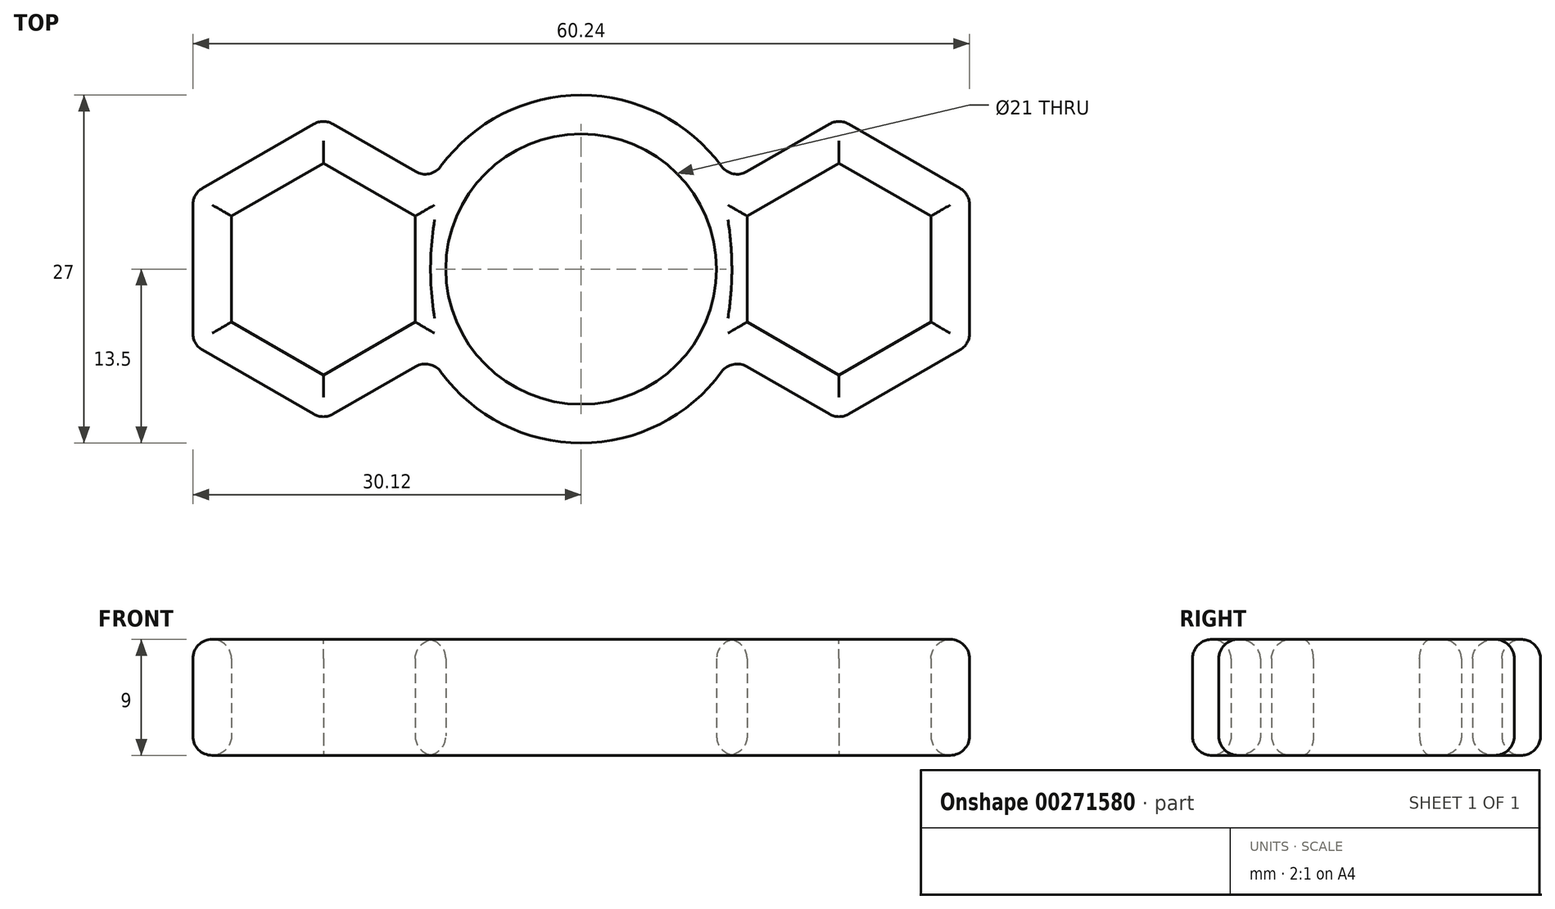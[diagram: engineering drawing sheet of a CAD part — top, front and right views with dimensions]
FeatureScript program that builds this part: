
annotation { "Feature Type Name" : "Feature", "Feature Type Description" : "" }
export const myFeature = defineFeature(function(context is Context, id is Id, definition is map)
    precondition{}
    {
        {
            var Q0;
            Q0=qCreatedBy(makeId("Top.planeOp"),FACE);
            var sketch = newSketch(context, id + "F0", { "sketchPlane" : qUnion([Q0])});
            skCircle(sketch, "E0", {"center": v(0, 0) * mm, "radius": 10.5 * mm});
            skCircle(sketch, "E1.cCircle", {"center": v(20, 0) * mm, "radius": 7.12 * mm, "construction": true});
            skLineSegment(sketch, "E1.0", {"start": v(12.87, -4.11) * mm, "end": v(12.87, 4.11) * mm});
            skLineSegment(sketch, "E1.1", {"start": v(12.87, 4.11) * mm, "end": v(20, 8.23) * mm});
            skLineSegment(sketch, "E1.2", {"start": v(20, 8.23) * mm, "end": v(27.13, 4.11) * mm});
            skLineSegment(sketch, "E1.3", {"start": v(27.13, 4.11) * mm, "end": v(27.13, -4.11) * mm});
            skLineSegment(sketch, "E1.4", {"start": v(27.13, -4.11) * mm, "end": v(20, -8.23) * mm});
            skLineSegment(sketch, "E1.5", {"start": v(20, -8.23) * mm, "end": v(12.87, -4.11) * mm});
            skPoint(sketch, "E1.0.midPoint", {"position": v(12.87, 0) * mm});
            skLineSegment(sketch, "E2", {"start": v(0, -8.9) * mm, "end": v(0, 12.72) * mm, "construction": true});
            skLineSegment(sketch, "E3", {"start": v(0, 12.72) * mm, "end": v(0, 9.77) * mm, "construction": true});
            skCircle(sketch, "E4.MirrorC", {"center": v(-20, 0) * mm, "radius": 7.12 * mm, "construction": true});
            skLineSegment(sketch, "E5.MirrorCS", {"start": v(-12.87, 4.11) * mm, "end": v(-20, 8.23) * mm});
            skLineSegment(sketch, "E6.MirrorCS", {"start": v(-27.13, 4.11) * mm, "end": v(-27.13, -4.11) * mm});
            skLineSegment(sketch, "E7.MirrorCS", {"start": v(-12.87, -4.11) * mm, "end": v(-12.87, 4.11) * mm});
            skPoint(sketch, "E8.MirrorP", {"position": v(-12.87, 0) * mm});
            skLineSegment(sketch, "E9.MirrorCS", {"start": v(-20, 8.23) * mm, "end": v(-27.13, 4.11) * mm});
            skLineSegment(sketch, "E10.MirrorCS", {"start": v(-20, -8.23) * mm, "end": v(-12.87, -4.11) * mm});
            skLineSegment(sketch, "E11.MirrorCS", {"start": v(-27.13, -4.11) * mm, "end": v(-20, -8.23) * mm});
            skArc(sketch, "E12.0", {"start": v(11.63, 6.86) * mm, "mid": v(0, 13.5) * mm, "end": v(-11.63, 6.86) * mm});
            skLineSegment(sketch, "E13.0", {"start": v(-20, 11.7) * mm, "end": v(-30.13, 5.85) * mm});
            skLineSegment(sketch, "E13.1", {"start": v(-30.13, -5.85) * mm, "end": v(-20, -11.7) * mm});
            skLineSegment(sketch, "E13.2", {"start": v(-20, -11.7) * mm, "end": v(-11.63, -6.86) * mm});
            skLineSegment(sketch, "E13.3", {"start": v(-30.13, 5.85) * mm, "end": v(-30.13, -5.85) * mm});
            skLineSegment(sketch, "E13.5", {"start": v(-11.63, 6.86) * mm, "end": v(-20, 11.7) * mm});
            skLineSegment(sketch, "E14.1", {"start": v(20, 11.7) * mm, "end": v(30.13, 5.85) * mm});
            skLineSegment(sketch, "E14.2", {"start": v(30.13, 5.85) * mm, "end": v(30.13, -5.85) * mm});
            skLineSegment(sketch, "E14.3", {"start": v(11.63, 6.86) * mm, "end": v(20, 11.7) * mm});
            skLineSegment(sketch, "E14.4", {"start": v(30.13, -5.85) * mm, "end": v(20, -11.7) * mm});
            skLineSegment(sketch, "E14.5", {"start": v(20, -11.7) * mm, "end": v(11.63, -6.86) * mm});
            skArc(sketch, "E15.trimOffspring", {"start": v(-11.63, -6.86) * mm, "mid": v(0, -13.5) * mm, "end": v(11.63, -6.86) * mm});
            skSolve(sketch);
        }
        {
            var Q0;
            Q0=makeQuery(id+"F0.imprint","IMPRINT",FACE,{"disambiguationData":[TD([[makeQuery(id+"F0.imprint","IMPRINT",EDGE,{"derivedFrom":sQuery(id+"F0.wireOp",EDGE,"E0")}),-1.0]])]});
            extrude(context, id + "F1", {"entities" : qUnion([Q0]), "depth" : 9 * mm});
        }
        {
            var Q0;
            Q0=makeQuery(id+"F1.opExtrude","CAP_EDGE",EDGE,{"disambiguationData":[OSD([sQuery(id+"F0.wireOp",EDGE,"E9.MirrorCS")])],"isStart":false});
            var Q1;
            Q1=makeQuery(id+"F1.opExtrude","CAP_EDGE",EDGE,{"disambiguationData":[OSD([sQuery(id+"F0.wireOp",EDGE,"E6.MirrorCS")])],"isStart":false});
            var Q2;
            Q2=makeQuery(id+"F1.opExtrude","CAP_EDGE",EDGE,{"disambiguationData":[OSD([sQuery(id+"F0.wireOp",EDGE,"E11.MirrorCS")])],"isStart":false});
            var Q3;
            Q3=makeQuery(id+"F1.opExtrude","CAP_EDGE",EDGE,{"disambiguationData":[OSD([sQuery(id+"F0.wireOp",EDGE,"E10.MirrorCS")])],"isStart":false});
            var Q4;
            Q4=makeQuery(id+"F1.opExtrude","CAP_EDGE",EDGE,{"disambiguationData":[OSD([sQuery(id+"F0.wireOp",EDGE,"E7.MirrorCS")])],"isStart":false});
            var Q5;
            Q5=makeQuery(id+"F1.opExtrude","CAP_EDGE",EDGE,{"disambiguationData":[OSD([sQuery(id+"F0.wireOp",EDGE,"E5.MirrorCS")])],"isStart":false});
            var Q6;
            Q6=makeQuery(id+"F1.opExtrude","CAP_EDGE",EDGE,{"disambiguationData":[OSD([sQuery(id+"F0.wireOp",EDGE,"E0")])],"isStart":false});
            var Q7;
            Q7=makeQuery(id+"F1.opExtrude","CAP_EDGE",EDGE,{"disambiguationData":[OSD([sQuery(id+"F0.wireOp",EDGE,"E1.0")])],"isStart":false});
            var Q8;
            Q8=makeQuery(id+"F1.opExtrude","CAP_EDGE",EDGE,{"disambiguationData":[OSD([sQuery(id+"F0.wireOp",EDGE,"E1.1")])],"isStart":false});
            var Q9;
            Q9=makeQuery(id+"F1.opExtrude","CAP_EDGE",EDGE,{"disambiguationData":[OSD([sQuery(id+"F0.wireOp",EDGE,"E1.2")])],"isStart":false});
            var Q10;
            Q10=makeQuery(id+"F1.opExtrude","CAP_EDGE",EDGE,{"disambiguationData":[OSD([sQuery(id+"F0.wireOp",EDGE,"E1.3")])],"isStart":false});
            var Q11;
            Q11=makeQuery(id+"F1.opExtrude","CAP_EDGE",EDGE,{"disambiguationData":[OSD([sQuery(id+"F0.wireOp",EDGE,"E1.4")])],"isStart":false});
            var Q12;
            Q12=makeQuery(id+"F1.opExtrude","CAP_EDGE",EDGE,{"disambiguationData":[OSD([sQuery(id+"F0.wireOp",EDGE,"E1.5")])],"isStart":false});
            var Q13;
            Q13=makeQuery(id+"F1.opExtrude","CAP_EDGE",EDGE,{"disambiguationData":[OSD([sQuery(id+"F0.wireOp",EDGE,"E6.MirrorCS")])],"isStart":true});
            var Q14;
            Q14=makeQuery(id+"F1.opExtrude","CAP_EDGE",EDGE,{"disambiguationData":[OSD([sQuery(id+"F0.wireOp",EDGE,"E11.MirrorCS")])],"isStart":true});
            var Q15;
            Q15=makeQuery(id+"F1.opExtrude","CAP_EDGE",EDGE,{"disambiguationData":[OSD([sQuery(id+"F0.wireOp",EDGE,"E10.MirrorCS")])],"isStart":true});
            var Q16;
            Q16=makeQuery(id+"F1.opExtrude","CAP_EDGE",EDGE,{"disambiguationData":[OSD([sQuery(id+"F0.wireOp",EDGE,"E7.MirrorCS")])],"isStart":true});
            var Q17;
            Q17=makeQuery(id+"F1.opExtrude","CAP_EDGE",EDGE,{"disambiguationData":[OSD([sQuery(id+"F0.wireOp",EDGE,"E5.MirrorCS")])],"isStart":true});
            var Q18;
            Q18=makeQuery(id+"F1.opExtrude","CAP_EDGE",EDGE,{"disambiguationData":[OSD([sQuery(id+"F0.wireOp",EDGE,"E9.MirrorCS")])],"isStart":true});
            var Q19;
            Q19=makeQuery(id+"F1.opExtrude","CAP_EDGE",EDGE,{"disambiguationData":[OSD([sQuery(id+"F0.wireOp",EDGE,"E0")])],"isStart":true});
            var Q20;
            Q20=makeQuery(id+"F1.opExtrude","CAP_EDGE",EDGE,{"disambiguationData":[OSD([sQuery(id+"F0.wireOp",EDGE,"E1.0")])],"isStart":true});
            var Q21;
            Q21=makeQuery(id+"F1.opExtrude","CAP_EDGE",EDGE,{"disambiguationData":[OSD([sQuery(id+"F0.wireOp",EDGE,"E1.5")])],"isStart":true});
            var Q22;
            Q22=makeQuery(id+"F1.opExtrude","CAP_EDGE",EDGE,{"disambiguationData":[OSD([sQuery(id+"F0.wireOp",EDGE,"E1.4")])],"isStart":true});
            var Q23;
            Q23=makeQuery(id+"F1.opExtrude","CAP_EDGE",EDGE,{"disambiguationData":[OSD([sQuery(id+"F0.wireOp",EDGE,"E1.3")])],"isStart":true});
            var Q24;
            Q24=makeQuery(id+"F1.opExtrude","CAP_EDGE",EDGE,{"disambiguationData":[OSD([sQuery(id+"F0.wireOp",EDGE,"E1.2")])],"isStart":true});
            var Q25;
            Q25=makeQuery(id+"F1.opExtrude","CAP_EDGE",EDGE,{"disambiguationData":[OSD([sQuery(id+"F0.wireOp",EDGE,"E1.1")])],"isStart":true});
            var Q26;
            Q26=makeQuery(id+"F1.opExtrude","CAP_FACE",FACE,{"disambiguationData":[OSD([sQuery(id+"F0.wireOp",EDGE,"E0"),sQuery(id+"F0.wireOp",EDGE,"E1.0"),sQuery(id+"F0.wireOp",EDGE,"E1.1"),sQuery(id+"F0.wireOp",EDGE,"E1.2"),sQuery(id+"F0.wireOp",EDGE,"E1.3"),sQuery(id+"F0.wireOp",EDGE,"E1.4"),sQuery(id+"F0.wireOp",EDGE,"E1.5"),sQuery(id+"F0.wireOp",EDGE,"E5.MirrorCS"),sQuery(id+"F0.wireOp",EDGE,"E6.MirrorCS"),sQuery(id+"F0.wireOp",EDGE,"E7.MirrorCS"),sQuery(id+"F0.wireOp",EDGE,"E9.MirrorCS"),sQuery(id+"F0.wireOp",EDGE,"E10.MirrorCS"),sQuery(id+"F0.wireOp",EDGE,"E11.MirrorCS"),sQuery(id+"F0.wireOp",EDGE,"E12.0"),sQuery(id+"F0.wireOp",EDGE,"E13.0"),sQuery(id+"F0.wireOp",EDGE,"E13.1"),sQuery(id+"F0.wireOp",EDGE,"E13.2"),sQuery(id+"F0.wireOp",EDGE,"E13.3"),sQuery(id+"F0.wireOp",EDGE,"E13.5"),sQuery(id+"F0.wireOp",EDGE,"E14.1"),sQuery(id+"F0.wireOp",EDGE,"E14.2"),sQuery(id+"F0.wireOp",EDGE,"E14.3"),sQuery(id+"F0.wireOp",EDGE,"E14.4"),sQuery(id+"F0.wireOp",EDGE,"E14.5"),sQuery(id+"F0.wireOp",EDGE,"E15.trimOffspring")])],"isStart":true});
            var Q27;
            Q27=makeQuery(id+"F1.opExtrude","CAP_FACE",FACE,{"disambiguationData":[OSD([sQuery(id+"F0.wireOp",EDGE,"E0"),sQuery(id+"F0.wireOp",EDGE,"E1.0"),sQuery(id+"F0.wireOp",EDGE,"E1.1"),sQuery(id+"F0.wireOp",EDGE,"E1.2"),sQuery(id+"F0.wireOp",EDGE,"E1.3"),sQuery(id+"F0.wireOp",EDGE,"E1.4"),sQuery(id+"F0.wireOp",EDGE,"E1.5"),sQuery(id+"F0.wireOp",EDGE,"E5.MirrorCS"),sQuery(id+"F0.wireOp",EDGE,"E6.MirrorCS"),sQuery(id+"F0.wireOp",EDGE,"E7.MirrorCS"),sQuery(id+"F0.wireOp",EDGE,"E9.MirrorCS"),sQuery(id+"F0.wireOp",EDGE,"E10.MirrorCS"),sQuery(id+"F0.wireOp",EDGE,"E11.MirrorCS"),sQuery(id+"F0.wireOp",EDGE,"E12.0"),sQuery(id+"F0.wireOp",EDGE,"E13.0"),sQuery(id+"F0.wireOp",EDGE,"E13.1"),sQuery(id+"F0.wireOp",EDGE,"E13.2"),sQuery(id+"F0.wireOp",EDGE,"E13.3"),sQuery(id+"F0.wireOp",EDGE,"E13.5"),sQuery(id+"F0.wireOp",EDGE,"E14.1"),sQuery(id+"F0.wireOp",EDGE,"E14.2"),sQuery(id+"F0.wireOp",EDGE,"E14.3"),sQuery(id+"F0.wireOp",EDGE,"E14.4"),sQuery(id+"F0.wireOp",EDGE,"E14.5"),sQuery(id+"F0.wireOp",EDGE,"E15.trimOffspring")])],"isStart":false});
            var Q28;
            Q28=makeQuery(id+"F1.opExtrude","SWEPT_EDGE",EDGE,{"disambiguationData":[OSD([sQuery(id+"F0.wireOp",EDGE,"E13.1"),sQuery(id+"F0.wireOp",EDGE,"E13.2")])]});
            var Q29;
            Q29=makeQuery(id+"F1.opExtrude","SWEPT_EDGE",EDGE,{"disambiguationData":[OSD([sQuery(id+"F0.wireOp",EDGE,"E13.1"),sQuery(id+"F0.wireOp",EDGE,"E13.3")])]});
            var Q30;
            Q30=makeQuery(id+"F1.opExtrude","SWEPT_EDGE",EDGE,{"disambiguationData":[OSD([sQuery(id+"F0.wireOp",EDGE,"E13.2"),sQuery(id+"F0.wireOp",EDGE,"E15.trimOffspring")])]});
            var Q31;
            Q31=makeQuery(id+"F1.opExtrude","SWEPT_EDGE",EDGE,{"disambiguationData":[OSD([sQuery(id+"F0.wireOp",EDGE,"E14.5"),sQuery(id+"F0.wireOp",EDGE,"E15.trimOffspring")])]});
            var Q32;
            Q32=makeQuery(id+"F1.opExtrude","SWEPT_EDGE",EDGE,{"disambiguationData":[OSD([sQuery(id+"F0.wireOp",EDGE,"E14.4"),sQuery(id+"F0.wireOp",EDGE,"E14.5")])]});
            var Q33;
            Q33=makeQuery(id+"F1.opExtrude","SWEPT_EDGE",EDGE,{"disambiguationData":[OSD([sQuery(id+"F0.wireOp",EDGE,"E14.2"),sQuery(id+"F0.wireOp",EDGE,"E14.4")])]});
            var Q34;
            Q34=makeQuery(id+"F1.opExtrude","SWEPT_EDGE",EDGE,{"disambiguationData":[OSD([sQuery(id+"F0.wireOp",EDGE,"E14.1"),sQuery(id+"F0.wireOp",EDGE,"E14.2")])]});
            var Q35;
            Q35=makeQuery(id+"F1.opExtrude","SWEPT_EDGE",EDGE,{"disambiguationData":[OSD([sQuery(id+"F0.wireOp",EDGE,"E14.1"),sQuery(id+"F0.wireOp",EDGE,"E14.3")])]});
            var Q36;
            Q36=makeQuery(id+"F1.opExtrude","SWEPT_EDGE",EDGE,{"disambiguationData":[OSD([sQuery(id+"F0.wireOp",EDGE,"E12.0"),sQuery(id+"F0.wireOp",EDGE,"E14.3")])]});
            var Q37;
            Q37=makeQuery(id+"F1.opExtrude","SWEPT_EDGE",EDGE,{"disambiguationData":[OSD([sQuery(id+"F0.wireOp",EDGE,"E12.0"),sQuery(id+"F0.wireOp",EDGE,"E13.5")])]});
            var Q38;
            Q38=makeQuery(id+"F1.opExtrude","SWEPT_EDGE",EDGE,{"disambiguationData":[OSD([sQuery(id+"F0.wireOp",EDGE,"E13.0"),sQuery(id+"F0.wireOp",EDGE,"E13.5")])]});
            var Q39;
            Q39=makeQuery(id+"F1.opExtrude","SWEPT_EDGE",EDGE,{"disambiguationData":[OSD([sQuery(id+"F0.wireOp",EDGE,"E13.0"),sQuery(id+"F0.wireOp",EDGE,"E13.3")])]});
            fillet(context, id + "F2", {"entities" : qUnion([Q0, Q1, Q2, Q3, Q4, Q5, Q6, Q7, Q8, Q9, Q10, Q11, Q12, Q13, Q14, Q15, Q16, Q17, Q18, Q19, Q20, Q21, Q22, Q23, Q24, Q25, Q26, Q27, Q28, Q29, Q30, Q31, Q32, Q33, Q34, Q35, Q36, Q37, Q38, Q39]), "radius" : 1.5 * mm, "tangentPropagation" : true, "allowEdgeOverflow" : false});
        }
    });
